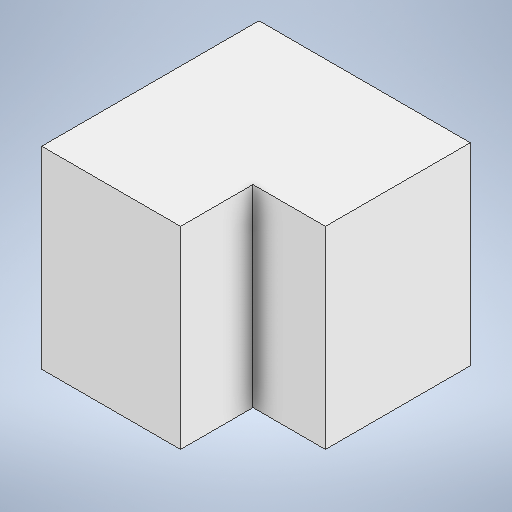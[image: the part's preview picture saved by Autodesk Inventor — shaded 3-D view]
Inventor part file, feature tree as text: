
AUTODESK INVENTOR PART (.ipt)
format: ipt  version: 2025 (Build 290162000, 162)  size: 226,304 bytes
history: native  units: in
note: dims shown in document units (in); Inventor stores cm internally (conversion verified against a paired STEP export)
features: extrude x1, sketch x1
ambient origin geometry x8: Origin, YZ Plane, XZ Plane, XY Plane, X Axis, Y Axis, Z Axis, Center Point
bodies: Solid1 (feature_tree)
feature tree (2):
  extrude  "Extrusion1"  Depth=36.0in
  sketch  "Sketch1"  dims[d7=32.0in d8=0.0in d9=36.0in d10=35.0in d11=24.0in d12=12.0in d13=23.0in]
